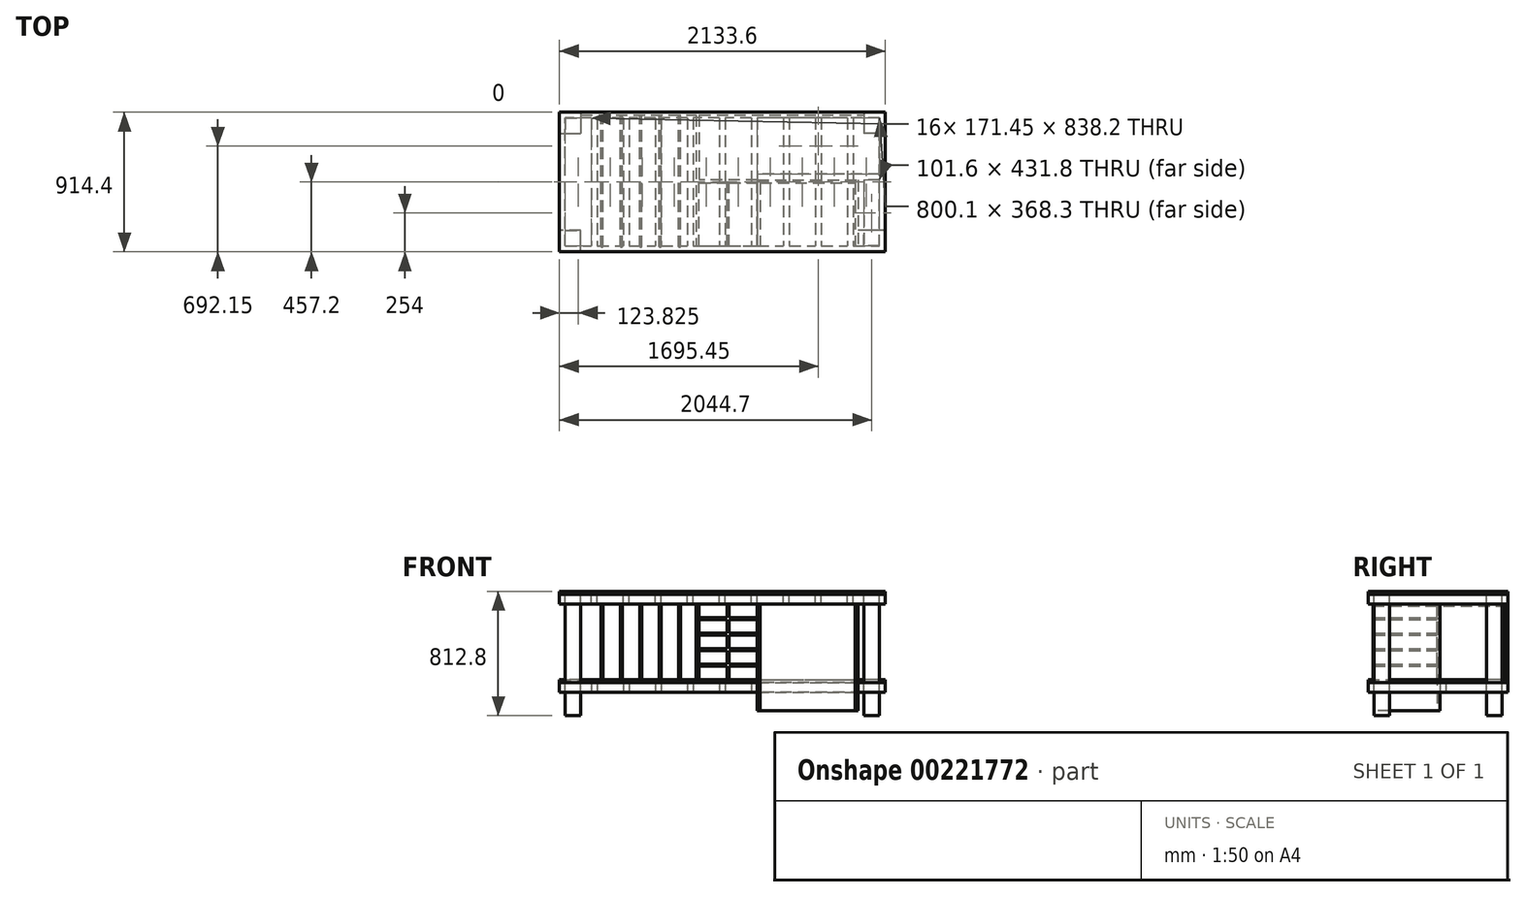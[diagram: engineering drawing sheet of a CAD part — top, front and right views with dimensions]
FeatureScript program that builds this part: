
annotation { "Feature Type Name" : "Feature", "Feature Type Description" : "" }
export const myFeature = defineFeature(function(context is Context, id is Id, definition is map)
    precondition{}
    {
        {
            var Q0;
            Q0=qCreatedBy(makeId("Top.planeOp"),FACE);
            var sketch = newSketch(context, id + "F0", { "sketchPlane" : qUnion([Q0])});
            skLineSegment(sketch, "E0.bottom", {"start": v(0, 0) * mm, "end": v(2133.6, 0) * mm});
            skLineSegment(sketch, "E0.top", {"start": v(0, -914.4) * mm, "end": v(2133.6, -914.4) * mm});
            skLineSegment(sketch, "E0.left", {"start": v(0, 0) * mm, "end": v(0, -914.4) * mm});
            skLineSegment(sketch, "E0.right", {"start": v(2133.6, 0) * mm, "end": v(2133.6, -914.4) * mm});
            skSolve(sketch);
        }
        {
            var Q0;
            Q0=makeQuery(id+"F0.imprint","IMPRINT",FACE,{"disambiguationData":[TD([[makeQuery(id+"F0.imprint","IMPRINT",EDGE,{"derivedFrom":sQuery(id+"F0.wireOp",EDGE,"E0.bottom")}),-1.0]])]});
            extrude(context, id + "F1", {"entities" : qUnion([Q0]), "oppositeDirection" : true, "depth" : 19.05 * mm});
        }
        {
            var Q0;
            Q0=makeQuery(id+"F1.opExtrude","CAP_FACE",FACE,{"disambiguationData":[OSD([sQuery(id+"F0.wireOp",EDGE,"E0.bottom"),sQuery(id+"F0.wireOp",EDGE,"E0.top"),sQuery(id+"F0.wireOp",EDGE,"E0.left"),sQuery(id+"F0.wireOp",EDGE,"E0.right")])],"isStart":false});
            var sketch = newSketch(context, id + "F2", { "sketchPlane" : qUnion([Q0])});
            skLineSegment(sketch, "E1.bottom", {"start": v(0, 914.4) * mm, "end": v(38.1, 914.4) * mm});
            skLineSegment(sketch, "E1.top", {"start": v(0, 0) * mm, "end": v(38.1, 0) * mm});
            skLineSegment(sketch, "E1.left", {"start": v(0, 914.4) * mm, "end": v(0, 0) * mm});
            skLineSegment(sketch, "E1.right", {"start": v(38.1, 914.4) * mm, "end": v(38.1, 0) * mm});
            skLineSegment(sketch, "E2.bottom", {"start": v(2133.6, 914.4) * mm, "end": v(2095.5, 914.4) * mm});
            skLineSegment(sketch, "E2.top", {"start": v(2133.6, 0) * mm, "end": v(2095.5, 0) * mm});
            skLineSegment(sketch, "E2.left", {"start": v(2133.6, 914.4) * mm, "end": v(2133.6, 0) * mm});
            skLineSegment(sketch, "E2.right", {"start": v(2095.5, 914.4) * mm, "end": v(2095.5, 0) * mm});
            skLineSegment(sketch, "E3.bottom", {"start": v(1085.85, 38.1) * mm, "end": v(1047.75, 38.1) * mm});
            skLineSegment(sketch, "E3.top", {"start": v(1085.85, 876.3) * mm, "end": v(1047.75, 876.3) * mm});
            skLineSegment(sketch, "E3.left", {"start": v(1085.85, 38.1) * mm, "end": v(1085.85, 876.3) * mm});
            skLineSegment(sketch, "E3.right", {"start": v(1047.75, 38.1) * mm, "end": v(1047.75, 876.3) * mm});
            skPoint(sketch, "E3.middle", {"position": v(1066.8, 457.2) * mm});
            skPoint(sketch, "E4.1.0.0", {"position": v(1276.35, 457.2) * mm});
            skLineSegment(sketch, "E4.1.0.1", {"start": v(1257.3, 38.1) * mm, "end": v(1257.3, 876.3) * mm});
            skLineSegment(sketch, "E4.1.0.2", {"start": v(1295.4, 38.1) * mm, "end": v(1295.4, 876.3) * mm});
            skLineSegment(sketch, "E4.1.0.3", {"start": v(1295.4, 876.3) * mm, "end": v(1257.3, 876.3) * mm});
            skLineSegment(sketch, "E4.1.0.4", {"start": v(1295.4, 38.1) * mm, "end": v(1257.3, 38.1) * mm});
            skPoint(sketch, "E4.2.0.0", {"position": v(1485.9, 457.2) * mm});
            skLineSegment(sketch, "E4.2.0.1", {"start": v(1466.85, 38.1) * mm, "end": v(1466.85, 876.3) * mm});
            skLineSegment(sketch, "E4.2.0.2", {"start": v(1504.95, 38.1) * mm, "end": v(1504.95, 876.3) * mm});
            skLineSegment(sketch, "E4.2.0.3", {"start": v(1504.95, 876.3) * mm, "end": v(1466.85, 876.3) * mm});
            skLineSegment(sketch, "E4.2.0.4", {"start": v(1504.95, 38.1) * mm, "end": v(1466.85, 38.1) * mm});
            skPoint(sketch, "E4.3.0.0", {"position": v(1695.45, 457.2) * mm});
            skLineSegment(sketch, "E4.3.0.1", {"start": v(1676.4, 38.1) * mm, "end": v(1676.4, 876.3) * mm});
            skLineSegment(sketch, "E4.3.0.2", {"start": v(1714.5, 38.1) * mm, "end": v(1714.5, 876.3) * mm});
            skLineSegment(sketch, "E4.3.0.3", {"start": v(1714.5, 876.3) * mm, "end": v(1676.4, 876.3) * mm});
            skLineSegment(sketch, "E4.3.0.4", {"start": v(1714.5, 38.1) * mm, "end": v(1676.4, 38.1) * mm});
            skPoint(sketch, "E4.4.0.0", {"position": v(1905, 457.2) * mm});
            skLineSegment(sketch, "E4.4.0.1", {"start": v(1885.95, 38.1) * mm, "end": v(1885.95, 876.3) * mm});
            skLineSegment(sketch, "E4.4.0.2", {"start": v(1924.05, 38.1) * mm, "end": v(1924.05, 876.3) * mm});
            skLineSegment(sketch, "E4.4.0.3", {"start": v(1924.05, 876.3) * mm, "end": v(1885.95, 876.3) * mm});
            skLineSegment(sketch, "E4.4.0.4", {"start": v(1924.05, 38.1) * mm, "end": v(1885.95, 38.1) * mm});
            skLineSegment(sketch, "E4.direction1", {"start": v(1047.75, 38.1) * mm, "end": v(1257.3, 38.1) * mm, "construction": true});
            skLineSegment(sketch, "E5.1.0.0", {"start": v(876.3, 38.1) * mm, "end": v(876.3, 876.3) * mm});
            skLineSegment(sketch, "E5.1.0.1", {"start": v(838.2, 38.1) * mm, "end": v(838.2, 876.3) * mm});
            skPoint(sketch, "E5.1.0.2", {"position": v(857.25, 457.2) * mm});
            skLineSegment(sketch, "E5.1.0.3", {"start": v(876.3, 38.1) * mm, "end": v(838.2, 38.1) * mm});
            skLineSegment(sketch, "E5.1.0.4", {"start": v(876.3, 876.3) * mm, "end": v(838.2, 876.3) * mm});
            skLineSegment(sketch, "E5.2.0.0", {"start": v(666.75, 38.1) * mm, "end": v(666.75, 876.3) * mm});
            skLineSegment(sketch, "E5.2.0.1", {"start": v(628.65, 38.1) * mm, "end": v(628.65, 876.3) * mm});
            skPoint(sketch, "E5.2.0.2", {"position": v(647.7, 457.2) * mm});
            skLineSegment(sketch, "E5.2.0.3", {"start": v(666.75, 38.1) * mm, "end": v(628.65, 38.1) * mm});
            skLineSegment(sketch, "E5.2.0.4", {"start": v(666.75, 876.3) * mm, "end": v(628.65, 876.3) * mm});
            skLineSegment(sketch, "E5.3.0.0", {"start": v(457.2, 38.1) * mm, "end": v(457.2, 876.3) * mm});
            skLineSegment(sketch, "E5.3.0.1", {"start": v(419.1, 38.1) * mm, "end": v(419.1, 876.3) * mm});
            skPoint(sketch, "E5.3.0.2", {"position": v(438.15, 457.2) * mm});
            skLineSegment(sketch, "E5.3.0.3", {"start": v(457.2, 38.1) * mm, "end": v(419.1, 38.1) * mm});
            skLineSegment(sketch, "E5.3.0.4", {"start": v(457.2, 876.3) * mm, "end": v(419.1, 876.3) * mm});
            skLineSegment(sketch, "E5.4.0.0", {"start": v(247.65, 38.1) * mm, "end": v(247.65, 876.3) * mm});
            skLineSegment(sketch, "E5.4.0.1", {"start": v(209.55, 38.1) * mm, "end": v(209.55, 876.3) * mm});
            skPoint(sketch, "E5.4.0.2", {"position": v(228.6, 457.2) * mm});
            skLineSegment(sketch, "E5.4.0.3", {"start": v(247.65, 38.1) * mm, "end": v(209.55, 38.1) * mm});
            skLineSegment(sketch, "E5.4.0.4", {"start": v(247.65, 876.3) * mm, "end": v(209.55, 876.3) * mm});
            skLineSegment(sketch, "E5.direction1", {"start": v(1047.75, 38.1) * mm, "end": v(838.2, 38.1) * mm, "construction": true});
            skLineSegment(sketch, "E6.bottom", {"start": v(38.1, 914.4) * mm, "end": v(2095.5, 914.4) * mm});
            skLineSegment(sketch, "E6.top", {"start": v(38.1, 876.3) * mm, "end": v(2095.5, 876.3) * mm});
            skLineSegment(sketch, "E6.left", {"start": v(38.1, 914.4) * mm, "end": v(38.1, 876.3) * mm});
            skLineSegment(sketch, "E6.right", {"start": v(2095.5, 914.4) * mm, "end": v(2095.5, 876.3) * mm});
            skLineSegment(sketch, "E7.bottom", {"start": v(2095.5, 0) * mm, "end": v(38.1, 0) * mm});
            skLineSegment(sketch, "E7.top", {"start": v(2095.5, 38.1) * mm, "end": v(38.1, 38.1) * mm});
            skLineSegment(sketch, "E7.left", {"start": v(2095.5, 0) * mm, "end": v(2095.5, 38.1) * mm});
            skLineSegment(sketch, "E7.right", {"start": v(38.1, 0) * mm, "end": v(38.1, 38.1) * mm});
            skSolve(sketch);
        }
        {
            var Q0;
            Q0 = qSketchRegion(id + "F2", true);
            var Q1;
            {var subQ0=sQuery(id+"F2.wireOp",EDGE,"E5.4.0.0");Q1=makeQuery(id+"F2.imprint","IMPRINT",FACE,{"disambiguationData":[TD([[makeQuery(id+"F2.imprint","IMPRINT",EDGE,{"derivedFrom":subQ0}),1.0]])]});}
            var Q2;
            {var subQ0=sQuery(id+"F2.wireOp",EDGE,"E5.3.0.0");Q2=makeQuery(id+"F2.imprint","IMPRINT",FACE,{"disambiguationData":[TD([[makeQuery(id+"F2.imprint","IMPRINT",EDGE,{"derivedFrom":subQ0}),1.0]])]});}
            var Q3;
            {var subQ0=sQuery(id+"F2.wireOp",EDGE,"E5.2.0.0");Q3=makeQuery(id+"F2.imprint","IMPRINT",FACE,{"disambiguationData":[TD([[makeQuery(id+"F2.imprint","IMPRINT",EDGE,{"derivedFrom":subQ0}),1.0]])]});}
            var Q4;
            {var subQ0=sQuery(id+"F2.wireOp",EDGE,"E5.1.0.0");Q4=makeQuery(id+"F2.imprint","IMPRINT",FACE,{"disambiguationData":[TD([[makeQuery(id+"F2.imprint","IMPRINT",EDGE,{"derivedFrom":subQ0}),1.0]])]});}
            var Q5;
            {var subQ0=sQuery(id+"F2.wireOp",EDGE,"E3.left");Q5=makeQuery(id+"F2.imprint","IMPRINT",FACE,{"disambiguationData":[TD([[makeQuery(id+"F2.imprint","IMPRINT",EDGE,{"derivedFrom":subQ0}),1.0]])]});}
            var Q6;
            {var subQ0=sQuery(id+"F2.wireOp",EDGE,"E4.1.0.1");Q6=makeQuery(id+"F2.imprint","IMPRINT",FACE,{"disambiguationData":[TD([[makeQuery(id+"F2.imprint","IMPRINT",EDGE,{"derivedFrom":subQ0}),-1.0]])]});}
            var Q7;
            {var subQ0=sQuery(id+"F2.wireOp",EDGE,"E4.2.0.1");Q7=makeQuery(id+"F2.imprint","IMPRINT",FACE,{"disambiguationData":[TD([[makeQuery(id+"F2.imprint","IMPRINT",EDGE,{"derivedFrom":subQ0}),-1.0]])]});}
            var Q8;
            {var subQ0=sQuery(id+"F2.wireOp",EDGE,"E4.3.0.1");Q8=makeQuery(id+"F2.imprint","IMPRINT",FACE,{"disambiguationData":[TD([[makeQuery(id+"F2.imprint","IMPRINT",EDGE,{"derivedFrom":subQ0}),-1.0]])]});}
            var Q9;
            {var subQ0=sQuery(id+"F2.wireOp",EDGE,"E4.4.0.1");Q9=makeQuery(id+"F2.imprint","IMPRINT",FACE,{"disambiguationData":[TD([[makeQuery(id+"F2.imprint","IMPRINT",EDGE,{"derivedFrom":subQ0}),-1.0]])]});}
            extrude(context, id + "F3", {"entities" : qUnion([Q0, Q1, Q2, Q3, Q4, Q5, Q6, Q7, Q8, Q9]), "depth" : 63.5 * mm});
        }
        {
            var Q0;
            Q0=makeQuery(id+"F1.opExtrude","CAP_FACE",FACE,{"disambiguationData":[OSD([sQuery(id+"F0.wireOp",EDGE,"E0.bottom"),sQuery(id+"F0.wireOp",EDGE,"E0.top"),sQuery(id+"F0.wireOp",EDGE,"E0.left"),sQuery(id+"F0.wireOp",EDGE,"E0.right")])],"isStart":false});
            var sketch = newSketch(context, id + "F4", { "sketchPlane" : qUnion([Q0])});
            skLineSegment(sketch, "E8.bottom", {"start": v(38.1, 876.3) * mm, "end": v(139.7, 876.3) * mm});
            skLineSegment(sketch, "E8.top", {"start": v(38.1, 774.7) * mm, "end": v(139.7, 774.7) * mm});
            skLineSegment(sketch, "E8.left", {"start": v(38.1, 876.3) * mm, "end": v(38.1, 774.7) * mm});
            skLineSegment(sketch, "E8.right", {"start": v(139.7, 876.3) * mm, "end": v(139.7, 774.7) * mm});
            skLineSegment(sketch, "E9", {"start": v(1066.8, 914.4) * mm, "end": v(1066.8, 0) * mm});
            skLineSegment(sketch, "E10", {"start": v(0, 457.2) * mm, "end": v(2133.6, 457.2) * mm});
            skLineSegment(sketch, "E11.MirrorCS", {"start": v(2095.5, 876.3) * mm, "end": v(1993.9, 876.3) * mm});
            skLineSegment(sketch, "E12.MirrorCS", {"start": v(2095.5, 774.7) * mm, "end": v(1993.9, 774.7) * mm});
            skLineSegment(sketch, "E13.MirrorCS", {"start": v(2095.5, 876.3) * mm, "end": v(2095.5, 774.7) * mm});
            skLineSegment(sketch, "E14.MirrorCS", {"start": v(1993.9, 876.3) * mm, "end": v(1993.9, 774.7) * mm});
            skLineSegment(sketch, "E15.MirrorCS", {"start": v(38.1, 38.1) * mm, "end": v(38.1, 139.7) * mm});
            skLineSegment(sketch, "E16.MirrorCS", {"start": v(139.7, 38.1) * mm, "end": v(139.7, 139.7) * mm});
            skLineSegment(sketch, "E17.MirrorCS", {"start": v(38.1, 139.7) * mm, "end": v(139.7, 139.7) * mm});
            skLineSegment(sketch, "E18.MirrorCS", {"start": v(38.1, 38.1) * mm, "end": v(139.7, 38.1) * mm});
            skLineSegment(sketch, "E19.MirrorCS", {"start": v(1993.9, 38.1) * mm, "end": v(1993.9, 139.7) * mm});
            skLineSegment(sketch, "E20.MirrorCS", {"start": v(2095.5, 38.1) * mm, "end": v(1993.9, 38.1) * mm});
            skLineSegment(sketch, "E21.MirrorCS", {"start": v(2095.5, 38.1) * mm, "end": v(2095.5, 139.7) * mm});
            skLineSegment(sketch, "E22.MirrorCS", {"start": v(2095.5, 139.7) * mm, "end": v(1993.9, 139.7) * mm});
            skSolve(sketch);
        }
        {
            var Q0;
            Q0 = qSketchRegion(id + "F4", true);
            extrude(context, id + "F5", {"entities" : qUnion([Q0]), "depth" : 793.75 * mm});
        }
        {
            var Q0;
            Q0=makeQuery(id+"F5.opExtrude","CAP_FACE",FACE,{"disambiguationData":[OSD([sQuery(id+"F4.wireOp",EDGE,"E13.MirrorCS"),sQuery(id+"F4.wireOp",EDGE,"E11.MirrorCS"),sQuery(id+"F4.wireOp",EDGE,"E12.MirrorCS"),sQuery(id+"F4.wireOp",EDGE,"E14.MirrorCS")])],"isStart":false});
            cPlane(context, id + "F6", {"entities" : qUnion([Q0]), "cplaneType" : CPlaneType.OFFSET, "offset" : 152.4 * mm, "oppositeDirection" : true, "width" : 152.4 * mm, "height" : 152.4 * mm});
        }
        {
            var Q0;
            Q0=qCreatedBy(id+"F6.planeOp",FACE);
            var sketch = newSketch(context, id + "F7", { "sketchPlane" : qUnion([Q0])});
            skLineSegment(sketch, "E23.bottom", {"start": v(0, 914.4) * mm, "end": v(38.1, 914.4) * mm});
            skLineSegment(sketch, "E23.top", {"start": v(0, 0) * mm, "end": v(38.1, 0) * mm});
            skLineSegment(sketch, "E23.left", {"start": v(0, 914.4) * mm, "end": v(0, 0) * mm});
            skLineSegment(sketch, "E23.right", {"start": v(38.1, 914.4) * mm, "end": v(38.1, 0) * mm});
            skLineSegment(sketch, "E24.right", {"start": v(2095.5, 914.4) * mm, "end": v(2095.5, 876.3) * mm});
            skLineSegment(sketch, "E25.bottom", {"start": v(1085.85, 38.1) * mm, "end": v(1047.75, 38.1) * mm});
            skLineSegment(sketch, "E25.top", {"start": v(1085.85, 876.3) * mm, "end": v(1047.75, 876.3) * mm});
            skLineSegment(sketch, "E25.left", {"start": v(1085.85, 38.1) * mm, "end": v(1085.85, 876.3) * mm});
            skLineSegment(sketch, "E25.right", {"start": v(1047.75, 38.1) * mm, "end": v(1047.75, 876.3) * mm});
            skPoint(sketch, "E25.middle", {"position": v(1066.8, 457.2) * mm});
            skPoint(sketch, "E26.1.0.0", {"position": v(1276.35, 457.2) * mm});
            skLineSegment(sketch, "E26.1.0.1", {"start": v(1257.3, 38.1) * mm, "end": v(1257.3, 876.3) * mm});
            skLineSegment(sketch, "E26.1.0.2", {"start": v(1295.4, 38.1) * mm, "end": v(1295.4, 876.3) * mm});
            skLineSegment(sketch, "E26.1.0.3", {"start": v(1295.4, 876.3) * mm, "end": v(1257.3, 876.3) * mm});
            skLineSegment(sketch, "E26.1.0.4", {"start": v(1295.4, 38.1) * mm, "end": v(1257.3, 38.1) * mm});
            skPoint(sketch, "E26.2.0.0", {"position": v(1485.9, 457.2) * mm});
            skPoint(sketch, "E26.3.0.0", {"position": v(1695.45, 457.2) * mm});
            skPoint(sketch, "E26.4.0.0", {"position": v(1905, 457.2) * mm});
            skLineSegment(sketch, "E26.direction1", {"start": v(1047.75, 38.1) * mm, "end": v(1257.3, 38.1) * mm, "construction": true});
            skLineSegment(sketch, "E27.1.0.0", {"start": v(876.3, 38.1) * mm, "end": v(876.3, 876.3) * mm});
            skLineSegment(sketch, "E27.1.0.1", {"start": v(838.2, 38.1) * mm, "end": v(838.2, 876.3) * mm});
            skPoint(sketch, "E27.1.0.2", {"position": v(857.25, 457.2) * mm});
            skLineSegment(sketch, "E27.1.0.3", {"start": v(876.3, 38.1) * mm, "end": v(838.2, 38.1) * mm});
            skLineSegment(sketch, "E27.1.0.4", {"start": v(876.3, 876.3) * mm, "end": v(838.2, 876.3) * mm});
            skLineSegment(sketch, "E27.2.0.0", {"start": v(666.75, 38.1) * mm, "end": v(666.75, 876.3) * mm});
            skLineSegment(sketch, "E27.2.0.1", {"start": v(628.65, 38.1) * mm, "end": v(628.65, 876.3) * mm});
            skPoint(sketch, "E27.2.0.2", {"position": v(647.7, 457.2) * mm});
            skLineSegment(sketch, "E27.2.0.3", {"start": v(666.75, 38.1) * mm, "end": v(628.65, 38.1) * mm});
            skLineSegment(sketch, "E27.2.0.4", {"start": v(666.75, 876.3) * mm, "end": v(628.65, 876.3) * mm});
            skLineSegment(sketch, "E27.3.0.0", {"start": v(457.2, 38.1) * mm, "end": v(457.2, 876.3) * mm});
            skLineSegment(sketch, "E27.3.0.1", {"start": v(419.1, 38.1) * mm, "end": v(419.1, 876.3) * mm});
            skPoint(sketch, "E27.3.0.2", {"position": v(438.15, 457.2) * mm});
            skLineSegment(sketch, "E27.3.0.3", {"start": v(457.2, 38.1) * mm, "end": v(419.1, 38.1) * mm});
            skLineSegment(sketch, "E27.3.0.4", {"start": v(457.2, 876.3) * mm, "end": v(419.1, 876.3) * mm});
            skLineSegment(sketch, "E27.4.0.0", {"start": v(247.65, 38.1) * mm, "end": v(247.65, 876.3) * mm});
            skLineSegment(sketch, "E27.4.0.1", {"start": v(209.55, 38.1) * mm, "end": v(209.55, 876.3) * mm});
            skPoint(sketch, "E27.4.0.2", {"position": v(228.6, 457.2) * mm});
            skLineSegment(sketch, "E27.4.0.3", {"start": v(247.65, 38.1) * mm, "end": v(209.55, 38.1) * mm});
            skLineSegment(sketch, "E27.4.0.4", {"start": v(247.65, 876.3) * mm, "end": v(209.55, 876.3) * mm});
            skLineSegment(sketch, "E27.direction1", {"start": v(1047.75, 38.1) * mm, "end": v(838.2, 38.1) * mm, "construction": true});
            skLineSegment(sketch, "E28.bottom", {"start": v(38.1, 914.4) * mm, "end": v(1295.4, 914.4) * mm});
            skLineSegment(sketch, "E28.top", {"start": v(38.1, 876.3) * mm, "end": v(1295.4, 876.3) * mm});
            skLineSegment(sketch, "E28.left", {"start": v(38.1, 914.4) * mm, "end": v(38.1, 876.3) * mm});
            skLineSegment(sketch, "E29.bottom", {"start": v(2095.5, 0) * mm, "end": v(38.1, 0) * mm});
            skLineSegment(sketch, "E29.top", {"start": v(2095.5, 38.1) * mm, "end": v(38.1, 38.1) * mm});
            skLineSegment(sketch, "E29.left", {"start": v(2095.5, 0) * mm, "end": v(2095.5, 38.1) * mm});
            skLineSegment(sketch, "E29.right", {"start": v(38.1, 0) * mm, "end": v(38.1, 38.1) * mm});
            skLineSegment(sketch, "E30.trimOffspring", {"start": v(2095.5, 38.1) * mm, "end": v(2095.5, 0) * mm});
            skLineSegment(sketch, "E31", {"start": v(2095.5, 876.3) * mm, "end": v(1993.9, 876.3) * mm});
            skLineSegment(sketch, "E32.left", {"start": v(2095.5, 914.4) * mm, "end": v(2095.5, 406.4) * mm});
            skLineSegment(sketch, "E33.bottom", {"start": v(2095.5, 406.4) * mm, "end": v(1295.4, 406.4) * mm});
            skLineSegment(sketch, "E33.top", {"start": v(2095.5, 444.5) * mm, "end": v(1955.8, 444.5) * mm});
            skLineSegment(sketch, "E33.left", {"start": v(2095.5, 406.4) * mm, "end": v(2095.5, 444.5) * mm});
            skLineSegment(sketch, "E33.right", {"start": v(1295.4, 406.4) * mm, "end": v(1295.4, 444.5) * mm});
            skLineSegment(sketch, "E34.bottom", {"start": v(1955.8, 444.5) * mm, "end": v(1993.9, 444.5) * mm});
            skLineSegment(sketch, "E34.top", {"start": v(1955.8, 914.4) * mm, "end": v(1993.9, 914.4) * mm});
            skLineSegment(sketch, "E34.left", {"start": v(1955.8, 444.5) * mm, "end": v(1955.8, 914.4) * mm});
            skLineSegment(sketch, "E34.right", {"start": v(1993.9, 444.5) * mm, "end": v(1993.9, 914.4) * mm});
            skLineSegment(sketch, "E35.trimOffspring", {"start": v(1955.8, 914.4) * mm, "end": v(2095.5, 914.4) * mm});
            skLineSegment(sketch, "E36", {"start": v(1295.4, 876.3) * mm, "end": v(1295.4, 914.4) * mm});
            skLineSegment(sketch, "E37", {"start": v(1295.4, 444.5) * mm, "end": v(2095.5, 444.5) * mm});
            skLineSegment(sketch, "E38.bottom", {"start": v(2095.5, 0) * mm, "end": v(2133.6, 0) * mm});
            skLineSegment(sketch, "E38.top", {"start": v(2095.5, 914.4) * mm, "end": v(2133.6, 914.4) * mm});
            skLineSegment(sketch, "E38.left", {"start": v(2095.5, 0) * mm, "end": v(2095.5, 914.4) * mm});
            skLineSegment(sketch, "E38.right", {"start": v(2133.6, 0) * mm, "end": v(2133.6, 914.4) * mm});
            skLineSegment(sketch, "E39.bottom", {"start": v(1504.95, 38.1) * mm, "end": v(1466.85, 38.1) * mm});
            skLineSegment(sketch, "E39.left", {"start": v(1504.95, 38.1) * mm, "end": v(1504.95, 406.4) * mm});
            skLineSegment(sketch, "E39.right", {"start": v(1466.85, 38.1) * mm, "end": v(1466.85, 406.4) * mm});
            skLineSegment(sketch, "E40.bottom", {"start": v(1714.5, 38.1) * mm, "end": v(1676.4, 38.1) * mm});
            skLineSegment(sketch, "E40.left", {"start": v(1714.5, 38.1) * mm, "end": v(1714.5, 406.4) * mm});
            skLineSegment(sketch, "E40.right", {"start": v(1676.4, 38.1) * mm, "end": v(1676.4, 406.4) * mm});
            skLineSegment(sketch, "E41.bottom", {"start": v(1924.05, 38.1) * mm, "end": v(1885.95, 38.1) * mm});
            skLineSegment(sketch, "E41.left", {"start": v(1924.05, 38.1) * mm, "end": v(1924.05, 406.4) * mm});
            skLineSegment(sketch, "E41.right", {"start": v(1885.95, 38.1) * mm, "end": v(1885.95, 406.4) * mm});
            skPoint(sketch, "E39.top.end.orphan", {"position": v(1466.85, 876.3) * mm});
            skPoint(sketch, "E39.top.start.orphan", {"position": v(1504.95, 876.3) * mm});
            skPoint(sketch, "E40.top.end.orphan", {"position": v(1676.4, 876.3) * mm});
            skPoint(sketch, "E40.top.start.orphan", {"position": v(1714.5, 876.3) * mm});
            skPoint(sketch, "E42.orphan", {"position": v(1885.95, 876.3) * mm});
            skPoint(sketch, "E43.orphan", {"position": v(1924.05, 876.3) * mm});
            skSolve(sketch);
        }
        {
            var Q0;
            Q0 = qSketchRegion(id + "F7", true);
            var Q1;
            {var subQ0=sQuery(id+"F7.wireOp",EDGE,"E27.4.0.0");Q1=makeQuery(id+"F7.imprint","IMPRINT",FACE,{"disambiguationData":[TD([[makeQuery(id+"F7.imprint","IMPRINT",EDGE,{"derivedFrom":subQ0}),1.0]])]});}
            var Q2;
            {var subQ0=sQuery(id+"F7.wireOp",EDGE,"E27.3.0.0");Q2=makeQuery(id+"F7.imprint","IMPRINT",FACE,{"disambiguationData":[TD([[makeQuery(id+"F7.imprint","IMPRINT",EDGE,{"derivedFrom":subQ0}),1.0]])]});}
            var Q3;
            {var subQ0=sQuery(id+"F7.wireOp",EDGE,"E27.2.0.0");Q3=makeQuery(id+"F7.imprint","IMPRINT",FACE,{"disambiguationData":[TD([[makeQuery(id+"F7.imprint","IMPRINT",EDGE,{"derivedFrom":subQ0}),1.0]])]});}
            var Q4;
            {var subQ0=sQuery(id+"F7.wireOp",EDGE,"E27.1.0.0");Q4=makeQuery(id+"F7.imprint","IMPRINT",FACE,{"disambiguationData":[TD([[makeQuery(id+"F7.imprint","IMPRINT",EDGE,{"derivedFrom":subQ0}),1.0]])]});}
            var Q5;
            {var subQ0=sQuery(id+"F7.wireOp",EDGE,"E25.left");Q5=makeQuery(id+"F7.imprint","IMPRINT",FACE,{"disambiguationData":[TD([[makeQuery(id+"F7.imprint","IMPRINT",EDGE,{"derivedFrom":subQ0}),1.0]])]});}
            var Q6;
            {var subQ0=sQuery(id+"F7.wireOp",EDGE,"E26.4.0.1");Q6=makeQuery(id+"F7.imprint","IMPRINT",FACE,{"disambiguationData":[TD([[makeQuery(id+"F7.imprint","IMPRINT",EDGE,{"derivedFrom":subQ0}),-1.0]])]});}
            var Q7;
            {var subQ0=sQuery(id+"F7.wireOp",EDGE,"E26.3.0.1");Q7=makeQuery(id+"F7.imprint","IMPRINT",FACE,{"disambiguationData":[TD([[makeQuery(id+"F7.imprint","IMPRINT",EDGE,{"derivedFrom":subQ0}),-1.0]])]});}
            var Q8;
            {var subQ0=sQuery(id+"F7.wireOp",EDGE,"E26.2.0.1");Q8=makeQuery(id+"F7.imprint","IMPRINT",FACE,{"disambiguationData":[TD([[makeQuery(id+"F7.imprint","IMPRINT",EDGE,{"derivedFrom":subQ0}),-1.0]])]});}
            var Q9;
            {var subQ0=sQuery(id+"F7.wireOp",EDGE,"E26.1.0.1");Q9=makeQuery(id+"F7.imprint","IMPRINT",FACE,{"disambiguationData":[TD([[makeQuery(id+"F7.imprint","IMPRINT",EDGE,{"derivedFrom":subQ0}),-1.0]])]});}
            var Q10;
            Q10=makeQuery(id+"F7.imprint","IMPRINT",FACE,{"disambiguationData":[TD([[makeQuery(id+"F7.imprint","IMPRINT",EDGE,{"derivedFrom":sQuery(id+"F7.wireOp",EDGE,"E39.bottom")}),-1.0]])]});
            var Q11;
            Q11=makeQuery(id+"F7.imprint","IMPRINT",FACE,{"disambiguationData":[TD([[makeQuery(id+"F7.imprint","IMPRINT",EDGE,{"derivedFrom":sQuery(id+"F7.wireOp",EDGE,"E40.bottom")}),-1.0]])]});
            var Q12;
            Q12=makeQuery(id+"F7.imprint","IMPRINT",FACE,{"disambiguationData":[TD([[makeQuery(id+"F7.imprint","IMPRINT",EDGE,{"derivedFrom":sQuery(id+"F7.wireOp",EDGE,"E41.bottom")}),-1.0]])]});
            extrude(context, id + "F8", {"entities" : qUnion([Q0, Q1, Q2, Q3, Q4, Q5, Q6, Q7, Q8, Q9, Q10, Q11, Q12]), "oppositeDirection" : true, "depth" : 63.5 * mm});
        }
        {
            var Q0;
            Q0=makeQuery(id+"F8.opExtrude","CAP_FACE",FACE,{"disambiguationData":[OSD([sQuery(id+"F7.wireOp",EDGE,"E23.bottom"),sQuery(id+"F7.wireOp",EDGE,"E23.top"),sQuery(id+"F7.wireOp",EDGE,"E23.left"),sQuery(id+"F7.wireOp",EDGE,"E23.right"),sQuery(id+"F7.wireOp",EDGE,"E25.left"),sQuery(id+"F7.wireOp",EDGE,"E25.right"),sQuery(id+"F7.wireOp",EDGE,"E26.1.0.1"),sQuery(id+"F7.wireOp",EDGE,"E26.1.0.2"),sQuery(id+"F7.wireOp",EDGE,"E27.1.0.0"),sQuery(id+"F7.wireOp",EDGE,"E27.1.0.1"),sQuery(id+"F7.wireOp",EDGE,"E27.2.0.0"),sQuery(id+"F7.wireOp",EDGE,"E27.2.0.1"),sQuery(id+"F7.wireOp",EDGE,"E27.3.0.0"),sQuery(id+"F7.wireOp",EDGE,"E27.3.0.1"),sQuery(id+"F7.wireOp",EDGE,"E27.4.0.0"),sQuery(id+"F7.wireOp",EDGE,"E27.4.0.1"),sQuery(id+"F7.wireOp",EDGE,"E28.bottom"),sQuery(id+"F7.wireOp",EDGE,"E28.top"),sQuery(id+"F7.wireOp",EDGE,"E29.bottom"),sQuery(id+"F7.wireOp",EDGE,"E29.top"),sQuery(id+"F7.wireOp",EDGE,"E31"),sQuery(id+"F7.wireOp",EDGE,"E33.bottom"),sQuery(id+"F7.wireOp",EDGE,"E34.left"),sQuery(id+"F7.wireOp",EDGE,"E34.right"),sQuery(id+"F7.wireOp",EDGE,"E35.trimOffspring"),sQuery(id+"F7.wireOp",EDGE,"E36"),sQuery(id+"F7.wireOp",EDGE,"E37"),sQuery(id+"F7.wireOp",EDGE,"E38.bottom"),sQuery(id+"F7.wireOp",EDGE,"E38.top"),sQuery(id+"F7.wireOp",EDGE,"E38.left"),sQuery(id+"F7.wireOp",EDGE,"E38.right"),sQuery(id+"F7.wireOp",EDGE,"E39.left"),sQuery(id+"F7.wireOp",EDGE,"E39.right"),sQuery(id+"F7.wireOp",EDGE,"E40.left"),sQuery(id+"F7.wireOp",EDGE,"E40.right"),sQuery(id+"F7.wireOp",EDGE,"E41.left"),sQuery(id+"F7.wireOp",EDGE,"E41.right")])],"isStart":false});
            var sketch = newSketch(context, id + "F9", { "sketchPlane" : qUnion([Q0])});
            skLineSegment(sketch, "E44", {"start": v(0, -139.7) * mm, "end": v(0, -774.7) * mm});
            skLineSegment(sketch, "E45", {"start": v(1295.4, -914.4) * mm, "end": v(1295.4, -444.5) * mm});
            skLineSegment(sketch, "E46", {"start": v(1295.4, -444.5) * mm, "end": v(1955.8, -444.5) * mm});
            skLineSegment(sketch, "E47", {"start": v(1955.8, -444.5) * mm, "end": v(1955.8, -774.7) * mm});
            skLineSegment(sketch, "E48", {"start": v(2133.6, -774.7) * mm, "end": v(2133.6, -139.7) * mm});
            skLineSegment(sketch, "E49", {"start": v(1993.9, 0) * mm, "end": v(139.7, 0) * mm});
            skLineSegment(sketch, "E50.right", {"start": v(139.7, -914.4) * mm, "end": v(139.7, -774.7) * mm});
            skLineSegment(sketch, "E51.top", {"start": v(2133.6, -139.7) * mm, "end": v(1993.9, -139.7) * mm});
            skLineSegment(sketch, "E51.right", {"start": v(1993.9, 0) * mm, "end": v(1993.9, -139.7) * mm});
            skLineSegment(sketch, "E52", {"start": v(139.7, -774.7) * mm, "end": v(0, -774.7) * mm});
            skLineSegment(sketch, "E53", {"start": v(139.7, 0) * mm, "end": v(139.7, -139.7) * mm});
            skLineSegment(sketch, "E54", {"start": v(0, -139.7) * mm, "end": v(139.7, -139.7) * mm});
            skLineSegment(sketch, "E55", {"start": v(2133.6, -774.7) * mm, "end": v(1993.9, -774.7) * mm});
            skLineSegment(sketch, "E56", {"start": v(139.7, -914.4) * mm, "end": v(1295.4, -914.4) * mm});
            skLineSegment(sketch, "E57", {"start": v(1993.9, -774.7) * mm, "end": v(1955.8, -774.7) * mm});
            skSolve(sketch);
        }
        {
            var Q0;
            Q0 = qSketchRegion(id + "F9", true);
            extrude(context, id + "F10", {"entities" : qUnion([Q0]), "depth" : 19.05 * mm});
        }
        {
            var Q0;
            Q0=makeQuery(id+"F10.opExtrude","CAP_FACE",FACE,{"disambiguationData":[OSD([sQuery(id+"F9.wireOp",EDGE,"E44"),sQuery(id+"F9.wireOp",EDGE,"E45"),sQuery(id+"F9.wireOp",EDGE,"E46"),sQuery(id+"F9.wireOp",EDGE,"E47"),sQuery(id+"F9.wireOp",EDGE,"5g02bo5s-HSkb-aqlp-8mdP-7zIEM0xrpJl6"),sQuery(id+"F9.wireOp",EDGE,"E48"),sQuery(id+"F9.wireOp",EDGE,"E49"),sQuery(id+"F9.wireOp",EDGE,"E50.right"),sQuery(id+"F9.wireOp",EDGE,"f2x244Uw-pRfw-9nqH-Hby6-cgYFjPfp4uoQ.right"),sQuery(id+"F9.wireOp",EDGE,"E51.top"),sQuery(id+"F9.wireOp",EDGE,"E51.right"),sQuery(id+"F9.wireOp",EDGE,"E52"),sQuery(id+"F9.wireOp",EDGE,"E53"),sQuery(id+"F9.wireOp",EDGE,"E54"),sQuery(id+"F9.wireOp",EDGE,"E55"),sQuery(id+"F9.wireOp",EDGE,"E56")])],"isStart":false});
            var sketch = newSketch(context, id + "F11", { "sketchPlane" : qUnion([Q0])});
            skLineSegment(sketch, "E58.bottom", {"start": v(1295.4, -444.5) * mm, "end": v(1314.45, -444.5) * mm});
            skLineSegment(sketch, "E58.left", {"start": v(1295.4, -444.5) * mm, "end": v(1295.4, -876.3) * mm});
            skLineSegment(sketch, "E58.right", {"start": v(1314.45, -444.5) * mm, "end": v(1314.45, -876.3) * mm});
            skLineSegment(sketch, "E59.bottom", {"start": v(1955.8, -444.5) * mm, "end": v(1936.75, -444.5) * mm});
            skLineSegment(sketch, "E59.left", {"start": v(1955.8, -444.5) * mm, "end": v(1955.8, -876.3) * mm});
            skLineSegment(sketch, "E59.right", {"start": v(1936.75, -444.5) * mm, "end": v(1936.75, -876.3) * mm});
            skLineSegment(sketch, "E60.bottom", {"start": v(1314.45, -444.5) * mm, "end": v(1936.75, -444.5) * mm});
            skLineSegment(sketch, "E60.top", {"start": v(1314.45, -463.55) * mm, "end": v(1936.75, -463.55) * mm});
            skLineSegment(sketch, "E60.left", {"start": v(1314.45, -444.5) * mm, "end": v(1314.45, -463.55) * mm});
            skLineSegment(sketch, "E60.right", {"start": v(1936.75, -444.5) * mm, "end": v(1936.75, -463.55) * mm});
            skLineSegment(sketch, "E61", {"start": v(1295.4, -876.3) * mm, "end": v(1314.45, -876.3) * mm});
            skLineSegment(sketch, "E62", {"start": v(1936.75, -876.3) * mm, "end": v(1955.8, -876.3) * mm});
            skSolve(sketch);
        }
        {
            var Q0;
            Q0=makeQuery(id+"F11.imprint","IMPRINT",FACE,{"disambiguationData":[TD([[makeQuery(id+"F11.imprint","IMPRINT",EDGE,{"derivedFrom":sQuery(id+"F11.wireOp",EDGE,"E58.bottom")}),-1.0]])]});
            var Q1;
            Q1=makeQuery(id+"F11.imprint","IMPRINT",FACE,{"disambiguationData":[TD([[makeQuery(id+"F11.imprint","IMPRINT",EDGE,{"derivedFrom":sQuery(id+"F11.wireOp",EDGE,"E60.bottom")}),-1.0]])]});
            var Q2;
            Q2=makeQuery(id+"F11.imprint","IMPRINT",FACE,{"disambiguationData":[TD([[makeQuery(id+"F11.imprint","IMPRINT",EDGE,{"derivedFrom":sQuery(id+"F11.wireOp",EDGE,"E59.bottom")}),-1.0]])]});
            extrude(context, id + "F12", {"entities" : qUnion([Q0, Q1, Q2]), "depth" : 495.3 * mm, "hasSecondDirection" : true, "secondDirectionOppositeDirection" : true, "secondDirectionDepth" : 203.2 * mm});
        }
        {
            var Q0;
            Q0=makeQuery(id+"F10.opExtrude","CAP_FACE",FACE,{"disambiguationData":[OSD([sQuery(id+"F9.wireOp",EDGE,"E44"),sQuery(id+"F9.wireOp",EDGE,"E45"),sQuery(id+"F9.wireOp",EDGE,"E46"),sQuery(id+"F9.wireOp",EDGE,"E47"),sQuery(id+"F9.wireOp",EDGE,"E48"),sQuery(id+"F9.wireOp",EDGE,"E49"),sQuery(id+"F9.wireOp",EDGE,"E50.right"),sQuery(id+"F9.wireOp",EDGE,"E51.top"),sQuery(id+"F9.wireOp",EDGE,"E51.right"),sQuery(id+"F9.wireOp",EDGE,"E52"),sQuery(id+"F9.wireOp",EDGE,"E53"),sQuery(id+"F9.wireOp",EDGE,"E54"),sQuery(id+"F9.wireOp",EDGE,"E55"),sQuery(id+"F9.wireOp",EDGE,"E56"),sQuery(id+"F9.wireOp",EDGE,"E57")])],"isStart":false});
            var sketch = newSketch(context, id + "F13", { "sketchPlane" : qUnion([Q0])});
            skLineSegment(sketch, "E63.bottom", {"start": v(139.7, 0) * mm, "end": v(1993.9, 0) * mm});
            skLineSegment(sketch, "E63.top", {"start": v(139.7, -19.05) * mm, "end": v(895.35, -19.05) * mm});
            skLineSegment(sketch, "E63.left", {"start": v(139.7, 0) * mm, "end": v(139.7, -19.05) * mm});
            skLineSegment(sketch, "E63.right", {"start": v(1993.9, 0) * mm, "end": v(1993.9, -19.05) * mm});
            skLineSegment(sketch, "E64.bottom", {"start": v(139.7, -19.05) * mm, "end": v(158.75, -19.05) * mm});
            skLineSegment(sketch, "E64.top", {"start": v(139.7, -876.3) * mm, "end": v(158.75, -876.3) * mm});
            skLineSegment(sketch, "E64.left", {"start": v(139.7, -19.05) * mm, "end": v(139.7, -876.3) * mm});
            skLineSegment(sketch, "E64.right", {"start": v(158.75, -19.05) * mm, "end": v(158.75, -876.3) * mm});
            skLineSegment(sketch, "E65.left", {"start": v(895.35, -19.05) * mm, "end": v(895.35, -444.5) * mm});
            skLineSegment(sketch, "E65.right", {"start": v(914.4, -19.05) * mm, "end": v(914.4, -444.5) * mm});
            skLineSegment(sketch, "E66.bottom", {"start": v(1295.4, -444.5) * mm, "end": v(914.4, -444.5) * mm});
            skLineSegment(sketch, "E66.top", {"start": v(1295.4, -463.55) * mm, "end": v(914.4, -463.55) * mm});
            skLineSegment(sketch, "E66.left", {"start": v(1295.4, -444.5) * mm, "end": v(1295.4, -463.55) * mm});
            skLineSegment(sketch, "E67.top", {"start": v(895.35, -876.3) * mm, "end": v(914.4, -876.3) * mm});
            skLineSegment(sketch, "E67.right", {"start": v(914.4, -463.55) * mm, "end": v(914.4, -876.3) * mm});
            skLineSegment(sketch, "E68.trimOffspring", {"start": v(914.4, -19.05) * mm, "end": v(1993.9, -19.05) * mm});
            skPoint(sketch, "E67.left.start.orphan", {"position": v(895.35, -463.55) * mm});
            skLineSegment(sketch, "E69", {"start": v(895.35, -444.5) * mm, "end": v(895.35, -876.3) * mm});
            skSolve(sketch);
        }
        {
            var Q0;
            {var subQ2=sQuery(id+"F13.wireOp",EDGE,"E64.bottom");Q0=makeQuery(id+"F13.imprint","IMPRINT",FACE,{"disambiguationData":[TD([[makeQuery(id+"F13.imprint","IMPRINT",EDGE,{"derivedFrom":subQ2}),-1.0]])]});}
            var Q1;
            Q1=makeQuery(id+"F13.imprint","IMPRINT",FACE,{"disambiguationData":[TD([[makeQuery(id+"F13.imprint","IMPRINT",EDGE,{"derivedFrom":sQuery(id+"F13.wireOp",EDGE,"E63.bottom")}),-1.0]])]});
            var Q2;
            Q2=makeQuery(id+"F13.imprint","IMPRINT",FACE,{"disambiguationData":[TD([[makeQuery(id+"F13.imprint","IMPRINT",EDGE,{"derivedFrom":sQuery(id+"F13.wireOp",EDGE,"rJvigvWu-ljxw-dKUC-88Z3-652DEOwcEQ0k.bottom")}),1.0]])]});
            extrude(context, id + "F14", {"entities" : qUnion([Q0, Q1, Q2]), "depth" : 495.3 * mm});
        }
        {
            var Q0;
            Q0=makeQuery(id+"F14.opExtrude","SWEPT_FACE",FACE,{"disambiguationData":[OSD([sQuery(id+"F13.wireOp",EDGE,"E63.top")])]});
            var sketch = newSketch(context, id + "F15", { "sketchPlane" : qUnion([Q0])});
            skLineSegment(sketch, "E70.bottom", {"start": v(273.05, -577.85) * mm, "end": v(285.75, -577.85) * mm});
            skLineSegment(sketch, "E70.top", {"start": v(273.05, -82.55) * mm, "end": v(285.75, -82.55) * mm});
            skLineSegment(sketch, "E70.left", {"start": v(273.05, -577.85) * mm, "end": v(273.05, -82.55) * mm});
            skLineSegment(sketch, "E70.right", {"start": v(285.75, -577.85) * mm, "end": v(285.75, -82.55) * mm});
            skLineSegment(sketch, "E71.1.0.0", {"start": v(412.75, -577.85) * mm, "end": v(412.75, -82.55) * mm});
            skLineSegment(sketch, "E71.1.0.1", {"start": v(400.05, -577.85) * mm, "end": v(400.05, -82.55) * mm});
            skLineSegment(sketch, "E71.1.0.2", {"start": v(400.05, -577.85) * mm, "end": v(412.75, -577.85) * mm});
            skLineSegment(sketch, "E71.1.0.3", {"start": v(400.05, -82.55) * mm, "end": v(412.75, -82.55) * mm});
            skLineSegment(sketch, "E71.2.0.0", {"start": v(539.75, -577.85) * mm, "end": v(539.75, -82.55) * mm});
            skLineSegment(sketch, "E71.2.0.1", {"start": v(527.05, -577.85) * mm, "end": v(527.05, -82.55) * mm});
            skLineSegment(sketch, "E71.2.0.2", {"start": v(527.05, -577.85) * mm, "end": v(539.75, -577.85) * mm});
            skLineSegment(sketch, "E71.2.0.3", {"start": v(527.05, -82.55) * mm, "end": v(539.75, -82.55) * mm});
            skLineSegment(sketch, "E71.3.0.0", {"start": v(666.75, -577.85) * mm, "end": v(666.75, -82.55) * mm});
            skLineSegment(sketch, "E71.3.0.1", {"start": v(654.05, -577.85) * mm, "end": v(654.05, -82.55) * mm});
            skLineSegment(sketch, "E71.3.0.2", {"start": v(654.05, -577.85) * mm, "end": v(666.75, -577.85) * mm});
            skLineSegment(sketch, "E71.3.0.3", {"start": v(654.05, -82.55) * mm, "end": v(666.75, -82.55) * mm});
            skLineSegment(sketch, "E71.4.0.0", {"start": v(793.75, -577.85) * mm, "end": v(793.75, -82.55) * mm});
            skLineSegment(sketch, "E71.4.0.1", {"start": v(781.05, -577.85) * mm, "end": v(781.05, -82.55) * mm});
            skLineSegment(sketch, "E71.4.0.2", {"start": v(781.05, -577.85) * mm, "end": v(793.75, -577.85) * mm});
            skLineSegment(sketch, "E71.4.0.3", {"start": v(781.05, -82.55) * mm, "end": v(793.75, -82.55) * mm});
            skLineSegment(sketch, "E71.direction1", {"start": v(273.05, -577.85) * mm, "end": v(400.05, -577.85) * mm, "construction": true});
            skLineSegment(sketch, "E72.bottom", {"start": v(158.75, -82.55) * mm, "end": v(895.35, -82.55) * mm});
            skLineSegment(sketch, "E72.top", {"start": v(158.75, -95.25) * mm, "end": v(895.35, -95.25) * mm});
            skLineSegment(sketch, "E72.left", {"start": v(158.75, -82.55) * mm, "end": v(158.75, -95.25) * mm});
            skLineSegment(sketch, "E72.right", {"start": v(895.35, -82.55) * mm, "end": v(895.35, -95.25) * mm});
            skSolve(sketch);
        }
        {
            var Q0;
            Q0=makeQuery(id+"F15.imprint","IMPRINT",FACE,{"disambiguationData":[TD([[makeQuery(id+"F15.imprint","IMPRINT",EDGE,{"derivedFrom":sQuery(id+"F15.wireOp",EDGE,"E71.1.0.0")}),1.0]])]});
            var Q1;
            Q1=makeQuery(id+"F15.imprint","IMPRINT",FACE,{"disambiguationData":[TD([[makeQuery(id+"F15.imprint","IMPRINT",EDGE,{"derivedFrom":sQuery(id+"F15.wireOp",EDGE,"E70.bottom")}),1.0]])]});
            var Q2;
            Q2=makeQuery(id+"F15.imprint","IMPRINT",FACE,{"disambiguationData":[TD([[makeQuery(id+"F15.imprint","IMPRINT",EDGE,{"derivedFrom":sQuery(id+"F15.wireOp",EDGE,"E71.2.0.0")}),1.0]])]});
            var Q3;
            Q3=makeQuery(id+"F15.imprint","IMPRINT",FACE,{"disambiguationData":[TD([[makeQuery(id+"F15.imprint","IMPRINT",EDGE,{"derivedFrom":sQuery(id+"F15.wireOp",EDGE,"E71.3.0.0")}),1.0]])]});
            var Q4;
            Q4=makeQuery(id+"F15.imprint","IMPRINT",FACE,{"disambiguationData":[TD([[makeQuery(id+"F15.imprint","IMPRINT",EDGE,{"derivedFrom":sQuery(id+"F15.wireOp",EDGE,"E71.4.0.0")}),1.0]])]});
            extrude(context, id + "F16", {"entities" : qUnion([Q0, Q1, Q2, Q3, Q4]), "depth" : 863.6 * mm});
        }
        {
            var Q0;
            Q0=makeQuery(id+"F14.opExtrude","SWEPT_FACE",FACE,{"disambiguationData":[OSD([sQuery(id+"F13.wireOp",EDGE,"E66.top")])]});
            var sketch = newSketch(context, id + "F17", { "sketchPlane" : qUnion([Q0])});
            skLineSegment(sketch, "E73.bottom", {"start": v(1111.25, -577.85) * mm, "end": v(1098.55, -577.85) * mm});
            skLineSegment(sketch, "E73.top", {"start": v(1111.25, -82.55) * mm, "end": v(1098.55, -82.55) * mm});
            skLineSegment(sketch, "E73.left", {"start": v(1111.25, -577.85) * mm, "end": v(1111.25, -82.55) * mm});
            skLineSegment(sketch, "E73.right", {"start": v(1098.55, -577.85) * mm, "end": v(1098.55, -82.55) * mm});
            skLineSegment(sketch, "E74.bottom", {"start": v(914.4, -476.25) * mm, "end": v(1295.4, -476.25) * mm});
            skLineSegment(sketch, "E74.top", {"start": v(914.4, -488.95) * mm, "end": v(1295.4, -488.95) * mm});
            skLineSegment(sketch, "E74.left", {"start": v(914.4, -476.25) * mm, "end": v(914.4, -488.95) * mm});
            skLineSegment(sketch, "E74.right", {"start": v(1295.4, -476.25) * mm, "end": v(1295.4, -488.95) * mm});
            skLineSegment(sketch, "E75.0.1.0", {"start": v(914.4, -374.65) * mm, "end": v(1295.4, -374.65) * mm});
            skLineSegment(sketch, "E75.0.1.1", {"start": v(914.4, -387.35) * mm, "end": v(1295.4, -387.35) * mm});
            skLineSegment(sketch, "E75.0.1.2", {"start": v(1295.4, -374.65) * mm, "end": v(1295.4, -387.35) * mm});
            skLineSegment(sketch, "E75.0.1.3", {"start": v(914.4, -374.65) * mm, "end": v(914.4, -387.35) * mm});
            skLineSegment(sketch, "E75.0.2.0", {"start": v(914.4, -273.05) * mm, "end": v(1295.4, -273.05) * mm});
            skLineSegment(sketch, "E75.0.2.1", {"start": v(914.4, -285.75) * mm, "end": v(1295.4, -285.75) * mm});
            skLineSegment(sketch, "E75.0.2.2", {"start": v(1295.4, -273.05) * mm, "end": v(1295.4, -285.75) * mm});
            skLineSegment(sketch, "E75.0.2.3", {"start": v(914.4, -273.05) * mm, "end": v(914.4, -285.75) * mm});
            skLineSegment(sketch, "E75.0.3.0", {"start": v(914.4, -171.45) * mm, "end": v(1295.4, -171.45) * mm});
            skLineSegment(sketch, "E75.0.3.1", {"start": v(914.4, -184.15) * mm, "end": v(1295.4, -184.15) * mm});
            skLineSegment(sketch, "E75.0.3.2", {"start": v(1295.4, -171.45) * mm, "end": v(1295.4, -184.15) * mm});
            skLineSegment(sketch, "E75.0.3.3", {"start": v(914.4, -171.45) * mm, "end": v(914.4, -184.15) * mm});
            skLineSegment(sketch, "E75.direction1", {"start": v(914.4, -476.25) * mm, "end": v(939.8, -476.25) * mm, "construction": true});
            skLineSegment(sketch, "E75.direction2", {"start": v(914.4, -476.25) * mm, "end": v(914.4, -374.65) * mm, "construction": true});
            skSolve(sketch);
        }
        {
            var Q0;
            {var subQ0=sQuery(id+"F17.wireOp",EDGE,"E73.top");Q0=makeQuery(id+"F17.imprint","IMPRINT",FACE,{"disambiguationData":[TD([[makeQuery(id+"F17.imprint","IMPRINT",EDGE,{"derivedFrom":subQ0}),1.0]])]});}
            var Q1;
            {var subQ5=sQuery(id+"F17.wireOp",EDGE,"E75.0.3.3");Q1=makeQuery(id+"F17.imprint","IMPRINT",FACE,{"disambiguationData":[TD([[makeQuery(id+"F17.imprint","IMPRINT",EDGE,{"derivedFrom":subQ5}),1.0]])]});}
            var Q2;
            {var subQ0=sQuery(id+"F17.wireOp",EDGE,"E75.0.3.1");var subQ1=sQuery(id+"F17.wireOp",EDGE,"E73.left");var subQ2=makeQuery(id+"F17.imprint","INTERSECT",VERTEX,{"derivedFrom":[subQ1,subQ0]});Q2=makeQuery(id+"F17.imprint","IMPRINT",FACE,{"disambiguationData":[TD([[makeQuery(id+"F17.imprint","IMPRINT",EDGE,{"disambiguationData":[TD([[subQ2,-1.0]])],"derivedFrom":subQ1}),1.0]])]});}
            var Q3;
            {var subQ5=sQuery(id+"F17.wireOp",EDGE,"E75.0.3.2");Q3=makeQuery(id+"F17.imprint","IMPRINT",FACE,{"disambiguationData":[TD([[makeQuery(id+"F17.imprint","IMPRINT",EDGE,{"derivedFrom":subQ5}),-1.0]])]});}
            var Q4;
            {var subQ0=sQuery(id+"F17.wireOp",EDGE,"E75.0.2.0");var subQ1=sQuery(id+"F17.wireOp",EDGE,"E73.left");var subQ2=makeQuery(id+"F17.imprint","INTERSECT",VERTEX,{"derivedFrom":[subQ1,subQ0]});Q4=makeQuery(id+"F17.imprint","IMPRINT",FACE,{"disambiguationData":[TD([[makeQuery(id+"F17.imprint","IMPRINT",EDGE,{"disambiguationData":[TD([[subQ2,-1.0]])],"derivedFrom":subQ1}),1.0]])]});}
            var Q5;
            {var subQ5=sQuery(id+"F17.wireOp",EDGE,"E75.0.2.3");Q5=makeQuery(id+"F17.imprint","IMPRINT",FACE,{"disambiguationData":[TD([[makeQuery(id+"F17.imprint","IMPRINT",EDGE,{"derivedFrom":subQ5}),1.0]])]});}
            var Q6;
            {var subQ0=sQuery(id+"F17.wireOp",EDGE,"E75.0.2.1");var subQ1=sQuery(id+"F17.wireOp",EDGE,"E73.left");var subQ2=makeQuery(id+"F17.imprint","INTERSECT",VERTEX,{"derivedFrom":[subQ1,subQ0]});Q6=makeQuery(id+"F17.imprint","IMPRINT",FACE,{"disambiguationData":[TD([[makeQuery(id+"F17.imprint","IMPRINT",EDGE,{"disambiguationData":[TD([[subQ2,-1.0]])],"derivedFrom":subQ1}),1.0]])]});}
            var Q7;
            {var subQ5=sQuery(id+"F17.wireOp",EDGE,"E75.0.2.2");Q7=makeQuery(id+"F17.imprint","IMPRINT",FACE,{"disambiguationData":[TD([[makeQuery(id+"F17.imprint","IMPRINT",EDGE,{"derivedFrom":subQ5}),-1.0]])]});}
            var Q8;
            {var subQ0=sQuery(id+"F17.wireOp",EDGE,"E75.0.1.0");var subQ1=sQuery(id+"F17.wireOp",EDGE,"E73.left");var subQ2=makeQuery(id+"F17.imprint","INTERSECT",VERTEX,{"derivedFrom":[subQ1,subQ0]});Q8=makeQuery(id+"F17.imprint","IMPRINT",FACE,{"disambiguationData":[TD([[makeQuery(id+"F17.imprint","IMPRINT",EDGE,{"disambiguationData":[TD([[subQ2,-1.0]])],"derivedFrom":subQ1}),1.0]])]});}
            var Q9;
            {var subQ5=sQuery(id+"F17.wireOp",EDGE,"E75.0.1.3");Q9=makeQuery(id+"F17.imprint","IMPRINT",FACE,{"disambiguationData":[TD([[makeQuery(id+"F17.imprint","IMPRINT",EDGE,{"derivedFrom":subQ5}),1.0]])]});}
            var Q10;
            {var subQ0=sQuery(id+"F17.wireOp",EDGE,"E75.0.1.1");var subQ1=sQuery(id+"F17.wireOp",EDGE,"E73.left");var subQ2=makeQuery(id+"F17.imprint","INTERSECT",VERTEX,{"derivedFrom":[subQ1,subQ0]});Q10=makeQuery(id+"F17.imprint","IMPRINT",FACE,{"disambiguationData":[TD([[makeQuery(id+"F17.imprint","IMPRINT",EDGE,{"disambiguationData":[TD([[subQ2,-1.0]])],"derivedFrom":subQ1}),1.0]])]});}
            var Q11;
            {var subQ5=sQuery(id+"F17.wireOp",EDGE,"E75.0.1.2");Q11=makeQuery(id+"F17.imprint","IMPRINT",FACE,{"disambiguationData":[TD([[makeQuery(id+"F17.imprint","IMPRINT",EDGE,{"derivedFrom":subQ5}),-1.0]])]});}
            var Q12;
            {var subQ0=sQuery(id+"F17.wireOp",EDGE,"E74.bottom");var subQ1=sQuery(id+"F17.wireOp",EDGE,"E73.left");var subQ2=makeQuery(id+"F17.imprint","INTERSECT",VERTEX,{"derivedFrom":[subQ1,subQ0]});Q12=makeQuery(id+"F17.imprint","IMPRINT",FACE,{"disambiguationData":[TD([[makeQuery(id+"F17.imprint","IMPRINT",EDGE,{"disambiguationData":[TD([[subQ2,-1.0]])],"derivedFrom":subQ1}),1.0]])]});}
            var Q13;
            {var subQ5=sQuery(id+"F17.wireOp",EDGE,"E74.left");Q13=makeQuery(id+"F17.imprint","IMPRINT",FACE,{"disambiguationData":[TD([[makeQuery(id+"F17.imprint","IMPRINT",EDGE,{"derivedFrom":subQ5}),1.0]])]});}
            var Q14;
            {var subQ0=sQuery(id+"F17.wireOp",EDGE,"E74.top");var subQ1=sQuery(id+"F17.wireOp",EDGE,"E73.left");var subQ2=makeQuery(id+"F17.imprint","INTERSECT",VERTEX,{"derivedFrom":[subQ1,subQ0]});Q14=makeQuery(id+"F17.imprint","IMPRINT",FACE,{"disambiguationData":[TD([[makeQuery(id+"F17.imprint","IMPRINT",EDGE,{"disambiguationData":[TD([[subQ2,-1.0]])],"derivedFrom":subQ1}),1.0]])]});}
            var Q15;
            {var subQ5=sQuery(id+"F17.wireOp",EDGE,"E74.right");Q15=makeQuery(id+"F17.imprint","IMPRINT",FACE,{"disambiguationData":[TD([[makeQuery(id+"F17.imprint","IMPRINT",EDGE,{"derivedFrom":subQ5}),-1.0]])]});}
            var Q16;
            {var subQ0=sQuery(id+"F17.wireOp",EDGE,"E73.bottom");Q16=makeQuery(id+"F17.imprint","IMPRINT",FACE,{"disambiguationData":[TD([[makeQuery(id+"F17.imprint","IMPRINT",EDGE,{"derivedFrom":subQ0}),-1.0]])]});}
            extrude(context, id + "F18", {"entities" : qUnion([Q0, Q1, Q2, Q3, Q4, Q5, Q6, Q7, Q8, Q9, Q10, Q11, Q12, Q13, Q14, Q15, Q16]), "depth" : 412.75 * mm});
        }
    });
